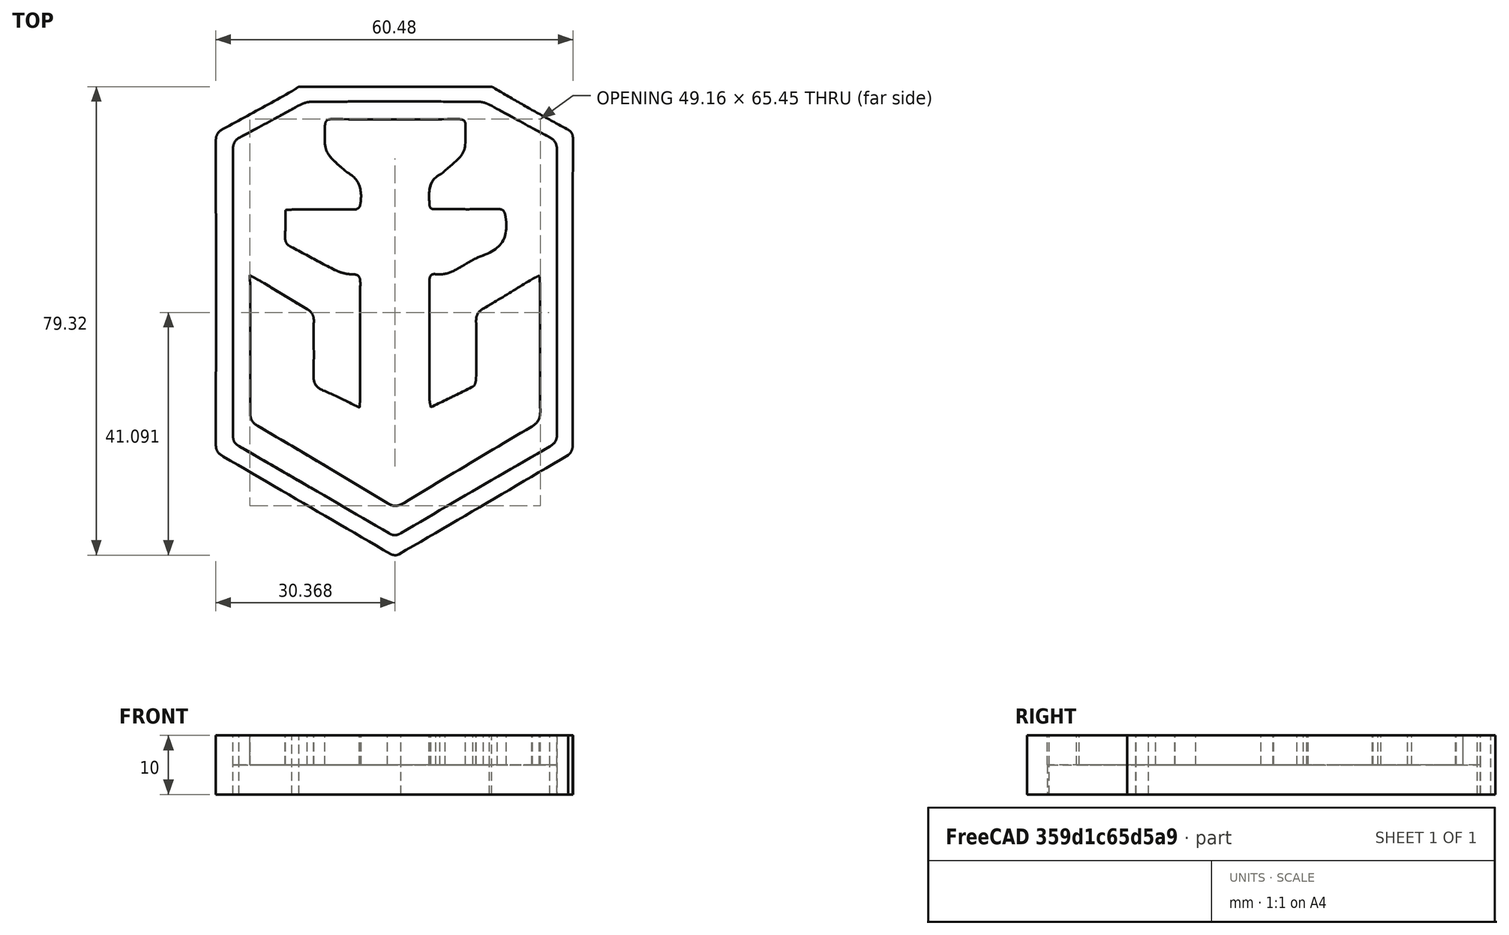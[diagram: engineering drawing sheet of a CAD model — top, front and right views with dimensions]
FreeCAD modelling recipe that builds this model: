
FCSTD DOCUMENT  (FreeCAD 0.16R6712 (Git))
Label: wowships
License: All rights reserved
LicenseURL: http://en.wikipedia.org/wiki/All_rights_reserved
objects: Part::Extrusion×4, Part::Feature×3, Part::Cut×1, Part::MultiFuse×1
note: 9 computed .brp shape members not serialized (recipe doc carries the construction recipe); baked Part::Feature solids carry a one-line shape summary decoded from their .brp

FEATURE [Part::Feature] Path001
  shape: bbox 60.48 x 79.35 x 2e-07 mm, 0 faces, 0 solids (baked)
FEATURE [Part::Feature] Path002
  shape: bbox 54.89 x 73.48 x 2e-07 mm, 0 faces, 0 solids (baked)
FEATURE [Part::Feature] Path005
  shape: bbox 49.16 x 65.54 x 2e-07 mm, 0 faces, 0 solids (baked)
FEATURE [Part::Extrusion] Extrude
  Base = -> Path005
  Dir = (0,0,10)
  Solid = true
FEATURE [Part::Extrusion] Extrude001
  Base = -> Path002
  Dir = (0,0,5)
  Solid = true
FEATURE [Part::Extrusion] Extrude002
  Base = -> Path002
  Dir = (0,0,12)
  Placement = pos=(0,0,5) rot=(0,0,1;0rad)
  Solid = true
FEATURE [Part::Extrusion] Extrude003
  Base = -> Path001
  Dir = (0,0,10)
  Solid = true
FEATURE [Part::Cut] Cut
  Base = -> Extrude003
  Tool = -> Extrude002
FEATURE [Part::MultiFuse] Fusion
  Shapes = -> [Extrude,Cut]
